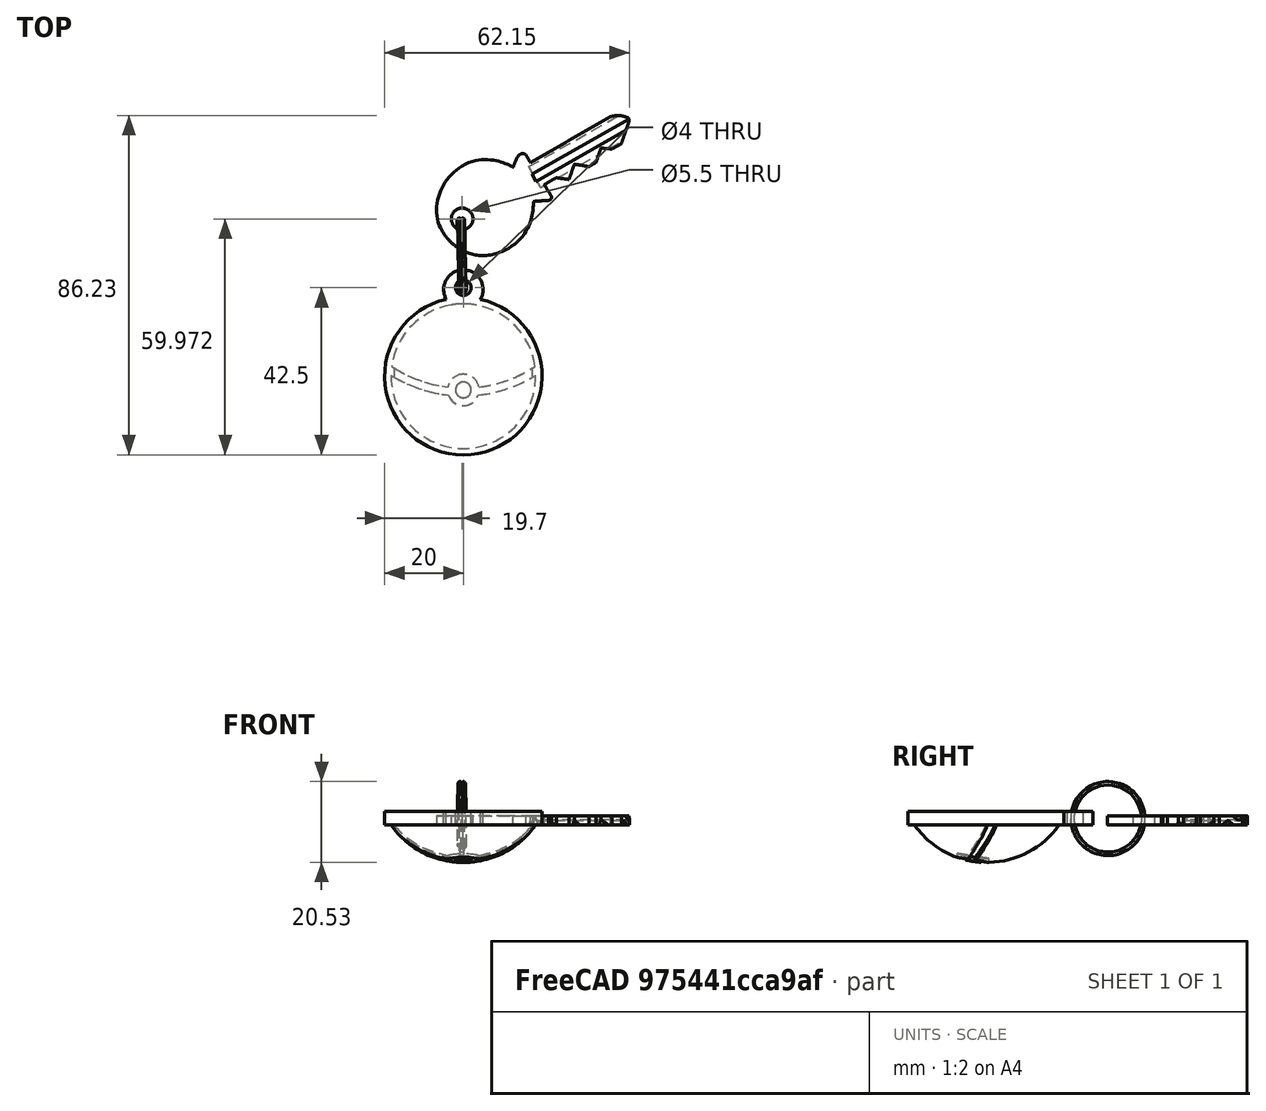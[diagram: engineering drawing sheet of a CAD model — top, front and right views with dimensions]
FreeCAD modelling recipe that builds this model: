
FCSTD DOCUMENT  (FreeCAD 0.14R3702 (Git))
Label: Pokellavero
License: CreativeCommons Attribution-ShareAlike
LicenseURL: http://creativecommons.org/licenses/by-sa/4.0/
objects: Part::Cut×6, Part::Cylinder×3, Part::MultiFuse×2, Part::Sphere×2, Part::Feature×2, Part::MultiCommon×1
note: 16 computed .brp shape members not serialized (recipe doc carries the construction recipe); baked Part::Feature solids carry a one-line shape summary decoded from their .brp

FEATURE [Part::MultiFuse] Fusion
FEATURE [Part::Sphere] Sphere
  Angle1 = -90
  Angle2 = -35
  Angle3 = 360
  Placement = pos=(0,0,13) rot=(0,0,1;0rad)
  Radius = 22.5
FEATURE [Part::Cylinder] Cylinder003  label="Cylinder005"
  Angle = 360
  Height = 18
  Placement = pos=(0,0,-35) rot=(0,0,1;0rad)
  Radius = 35
FEATURE [Part::Cylinder] Cylinder004  label="Cylinder001"
  Angle = 360
  Height = 18
  Placement = pos=(0,0,-35) rot=(0,0,1;0rad)
  Radius = 33
FEATURE [Part::Sphere] Sphere001
  Angle1 = -90
  Angle2 = -35
  Angle3 = 360
  Placement = pos=(0,0,13) rot=(0,0,1;0rad)
  Radius = 22.5
FEATURE [Part::Cut] Cut005
  Placement = pos=(0,0,1) rot=(0,0,1;0rad)
FEATURE [Part::MultiCommon] Common
FEATURE [Part::Cut] Cut002
  Base = -> Cylinder003
  Placement = pos=(30,0,17) rot=(0,0,1;0rad)
  Tool = -> Cylinder004
FEATURE [Part::Cut] Cut003
  Base = -> Cut002
  Placement = pos=(0,0,1) rot=(0,0,1;0rad)
  Tool = -> Sphere001
FEATURE [Part::Cut] Cut004
  Base = -> Sphere
  Tool = -> Cut003
FEATURE [Part::Cut] Cut006
  Base = -> Cut004
  Tool = -> Cut005
FEATURE [Part::MultiFuse] Fusion001
  Shapes = -> [Fusion,Common,Cut006]
FEATURE [Part::Cylinder] Cylinder  label="Cylinder002"
  Angle = 360
  Height = 4
  Placement = pos=(22.5,0,0) rot=(0,0,1;0rad)
  Radius = 2
FEATURE [Part::Cut] Cut007  label="Pokellavero"
  Base = -> Fusion001
  Placement = pos=(0,-6,0) rot=(0,0,1;1.5708rad)
  Tool = -> Cylinder
FEATURE [Part::Feature] Sweep001  label="key-ring-model"
  Placement = pos=(-1.2,24.7546,1.6391) rot=(0.333333,0.881918,0.333333;1.69612rad)
  shape: bbox 3.31 x 27.02 x 26.33 mm, 4 faces (baked)
FEATURE [Part::Feature] Cut008  label="key-model"
  Placement = pos=(-5.46976,31.0266,0) rot=(0,0,1;0.517888rad)
  shape: bbox 49.82 x 36.6 x 2.3 mm, 44 faces (baked)
